# Revit family: Lavatory_System-Single_Station-Sloan-ELC-81000_Series
name_source: partatom
category: Plumbing Fixtures
revit_build: Autodesk Revit 2015 (Build: 20140606_1530(x64)
units: mm (PartAtom-declared; Revit-internal decimal feet)

## types (19) — shared parameters
ADA Compliant = Yes
Assembly Code = D2010320
CW Connection = Yes
CWFU = 1.5
Cold Water Connection Radius = 1/4"
Default Elevation = 33 15/16"
Fixture Color = Consult your local Sloan Representative for color options
HW Connection = Yes
HWFU = 1.5
Hot Water Connection Radius = 1/4"
Manufacturer = SLOAN
Material = SloanStone-Sloan-WH-White
Operation = Sensor-Activated
Price = Prices may vary. Please consult Sloan Rep for most up-to-date price list.
Product Page URL = http://www.sloanvalve.com
Product data url = https://bimobject.com
Revised Date = 11/05/2012
Specification Sheet = http://www.sloanvalve.com
URL = http://www.sloanvalve.com
Vent Connection = No
WFU = 2
Warranty = 3 year (Limited)
Waste Connection = Yes
Waste Connection Radius = 3/4"

## per-type parameters (varying)
| type | Description | Faucet |
| ELC-81080 | Single Station SloanStone Lavatory without Faucet | Faucet-Electronic-Sloan-Optima-ETF-80_Series : ETF-80 |
| ELC-81085 | Single Station SloanStone Lavatory with EBF-85 Faucet | EBF-85 |
| ELC-81100 | Single Station SloanStone Lavatory with EAF-100 Faucet | Faucet-Electronic-Sloan-Optima-EAF-100 : EAF-100 |
| ELC-81150 | Single Station SloanStone Lavatory with EAF-150 Faucet | Faucet-Electronic-Sloan-Optima-EAF-100 : EAF-150 |
| ELC-81187 | Single Station SloanStone Lavatory with EBF-187 Faucet | EBF-187-4 : EBF-187 |
| ELC-81200 | Single Station SloanStone Lavatory with EAF-200 Faucet | Faucet-Electronic-Sloan-Lino-EAF-200 : EAF-200 |
| ELC-81250 | Single Station SloanStone Lavatory with EAF-250 Faucet | Faucet-Electronic-Sloan-Lino-EAF-200 : EAF-250 |
| ELC-81210 | Single Station SloanStone Lavatory with SF-2100 Faucet | Faucets-Electronic-Sloan-SF-2100_SF-2150 : SF-2100 |
| ELC-81215 | Single Station SloanStone Lavatory with SF-2150 Faucet | Faucets-Electronic-Sloan-SF-2100_SF-2150 : SF-2150 |
| ELC-81220 | Single Station SloanStone Lavatory with SF-2200 Faucet | Faucets-Electronic-Sloan-SF-2200_SF2250 : SF-2200 |
| ELC-81225 | Single Station SloanStone Lavatory with SF-2250 Faucet | Faucets-Electronic-Sloan-SF-2200_SF2250 : SF-2250 |
| ELC-81240 | Single Station SloanStone Lavatory with SF-2400 Faucet | Faucets-Electronic-Sloan-SF-2400_SF-2450 : SF-2400 |
| ELC-81245 | Single Station SloanStone Lavatory with SF-2450 Faucet | Faucets-Electronic-Sloan-SF-2400_SF-2450 : SF-2450 |
| ELC-81275 | Single Station SloanStone Lavatory with EAF-275 Faucet | Faucet-Sensor_Activated-Sloan-SOLIS-EAF_275 : EAF-275 |
| ELC-81610 | Single Station SloanStone Lavatory with ETF-610 Faucet | Faucet-Electronic-Sloan-Optima : ETF-610 |
| ELC-81615 | Single Station SloanStone Lavatory with EBF-615 Faucet | Faucet-Electronic-Sloan-Optima : EBF-615 |
| ELC-81700 | Single Station SloanStone Lavatory with ETF-700 Faucet | Faucet-Electronic-Sloan-Optima-700_Series : ETF-700 |
| ELC-81750 | Single Station SloanStone Lavatory with EBF-750 Faucet | Faucet-Electronic-Sloan-Optima-700_Series : EBF-750 |
| ELC-81880 | Single Station SloanStone Lavatory with ETF-880 Faucet | Faucet-Electronic-Sloan-Optima-ETF-880 : ETF-880 |

note: column(s) folded — value = type name in every type: Model

## geometry (parser evidence)
native form markers: Sweep x30
no freeform markers — native parametric forms only
